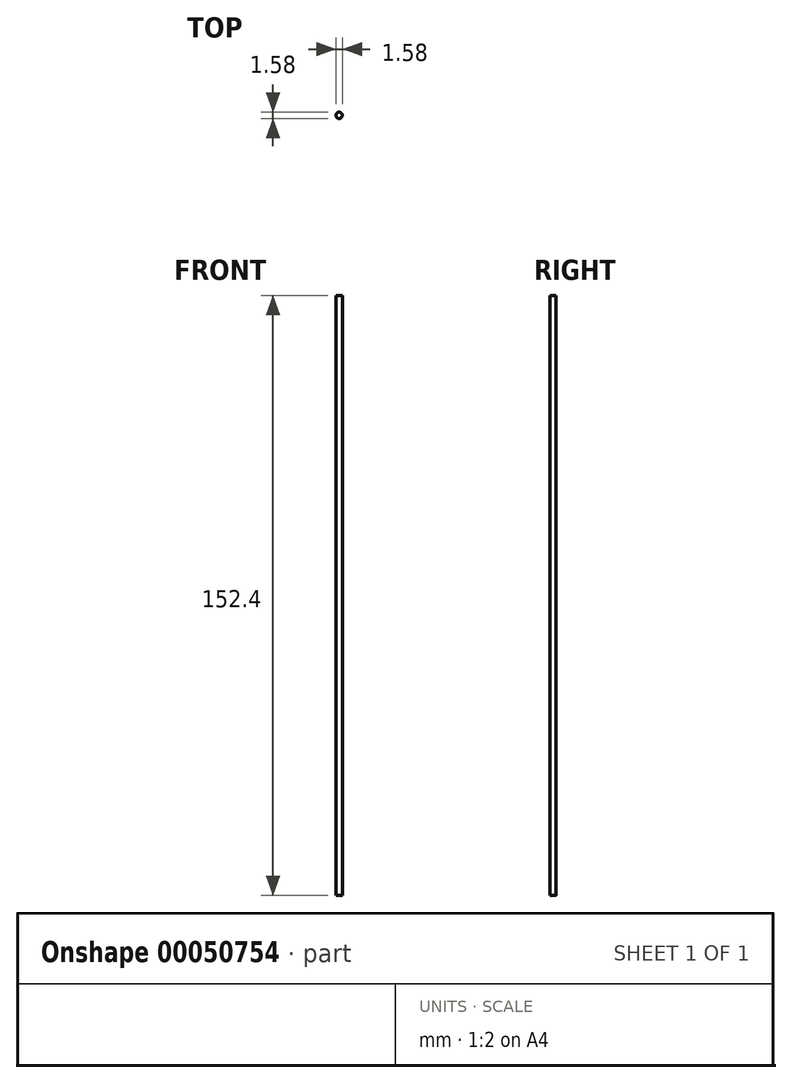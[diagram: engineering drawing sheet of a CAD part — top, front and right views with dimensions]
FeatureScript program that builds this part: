
annotation { "Feature Type Name" : "Feature", "Feature Type Description" : "" }
export const myFeature = defineFeature(function(context is Context, id is Id, definition is map)
    precondition{}
    {
        {
            var Q0;
            Q0=qCreatedBy(makeId("Top.planeOp"),FACE);
            var sketch = newSketch(context, id + "F0", { "sketchPlane" : qUnion([Q0])});
            skCircle(sketch, "E0", {"center": v(0, 0) * mm, "radius": 0.8 * mm});
            skSolve(sketch);
        }
        {
            var Q0;
            Q0 = qSketchRegion(id + "F0", true);
            extrude(context, id + "F1", {"entities" : qUnion([Q0]), "depth" : 152.4 * mm});
        }
    });
